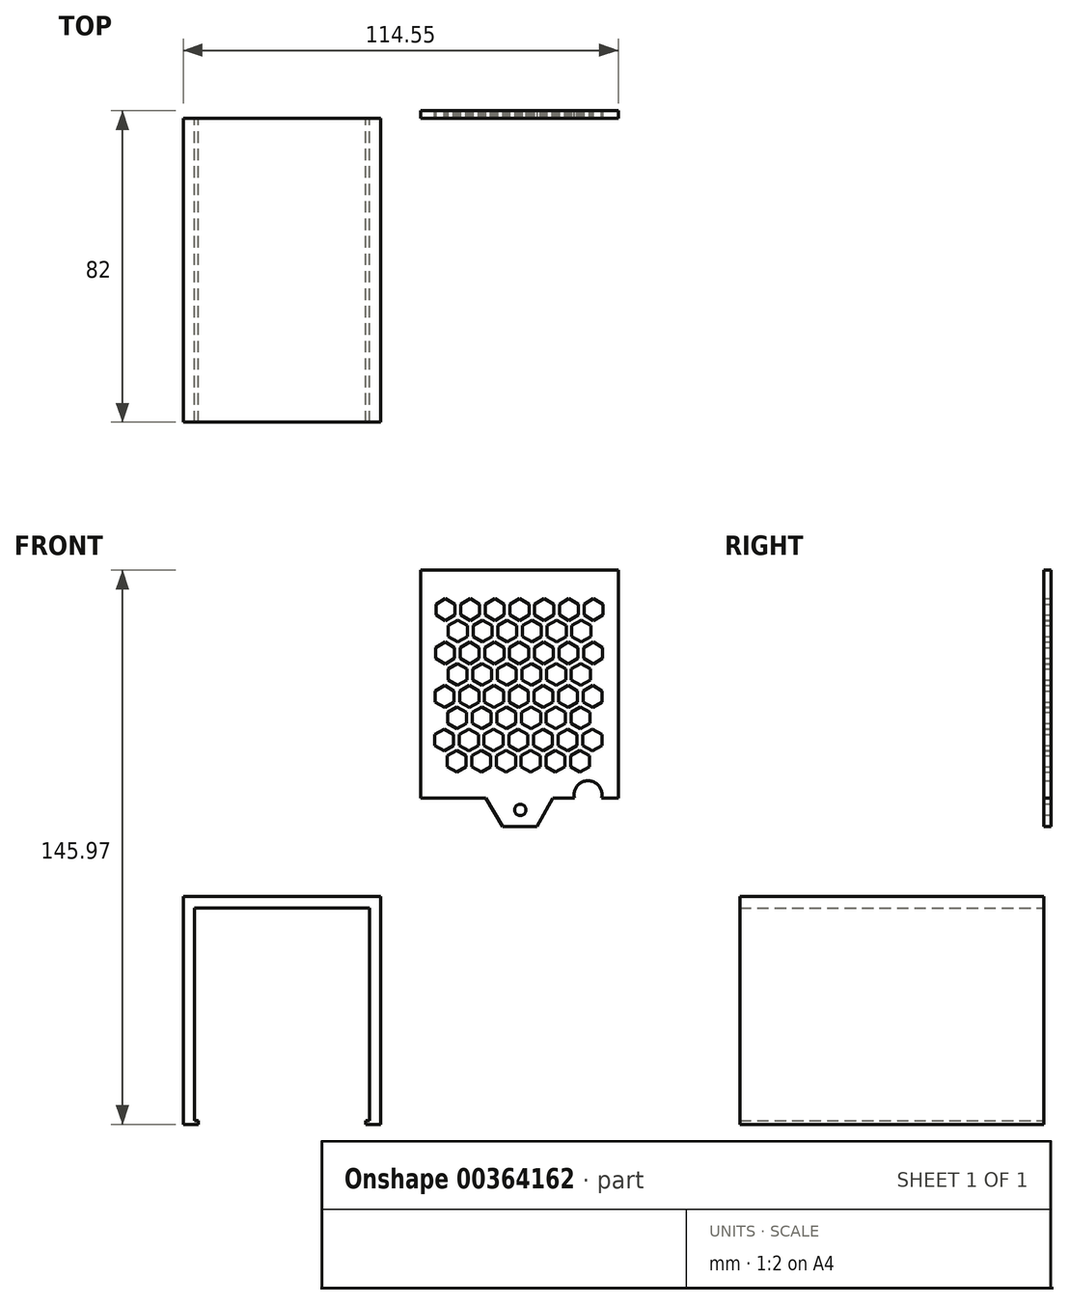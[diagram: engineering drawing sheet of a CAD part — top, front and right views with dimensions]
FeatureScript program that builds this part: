
annotation { "Feature Type Name" : "Feature", "Feature Type Description" : "" }
export const myFeature = defineFeature(function(context is Context, id is Id, definition is map)
    precondition{}
    {
        {
            var Q0;
            Q0=qCreatedBy(makeId("Front.planeOp"),FACE);
            var sketch = newSketch(context, id + "F0", { "sketchPlane" : qUnion([Q0])});
            skLineSegment(sketch, "E0", {"start": v(-25.2, -51.06) * mm, "end": v(-29.2, -51.06) * mm});
            skLineSegment(sketch, "E1", {"start": v(-29.2, -51.06) * mm, "end": v(-29.2, 8.94) * mm});
            skLineSegment(sketch, "E2", {"start": v(-29.2, 8.94) * mm, "end": v(22.8, 8.94) * mm});
            skLineSegment(sketch, "E3", {"start": v(22.8, 8.94) * mm, "end": v(22.8, -51.06) * mm});
            skLineSegment(sketch, "E4", {"start": v(22.8, -51.06) * mm, "end": v(18.8, -51.06) * mm});
            skLineSegment(sketch, "E5", {"start": v(18.8, -51.06) * mm, "end": v(18.8, -50.06) * mm});
            skLineSegment(sketch, "E6", {"start": v(18.8, -50.06) * mm, "end": v(19.8, -50.06) * mm});
            skLineSegment(sketch, "E7", {"start": v(19.8, -50.06) * mm, "end": v(19.8, 5.94) * mm});
            skLineSegment(sketch, "E8", {"start": v(19.8, 5.94) * mm, "end": v(-26.2, 5.94) * mm});
            skLineSegment(sketch, "E9", {"start": v(-26.2, 5.94) * mm, "end": v(-26.2, -50.06) * mm});
            skLineSegment(sketch, "E10", {"start": v(-26.2, -50.06) * mm, "end": v(-25.2, -50.06) * mm});
            skLineSegment(sketch, "E11", {"start": v(-25.2, -50.06) * mm, "end": v(-25.2, -51.06) * mm});
            skSolve(sketch);
        }
        {
            var Q0;
            Q0=makeQuery(id+"F0.imprint","IMPRINT",FACE,{"disambiguationData":[TD([[makeQuery(id+"F0.imprint","IMPRINT",EDGE,{"derivedFrom":sQuery(id+"F0.wireOp",EDGE,"E0")}),-1.0]])]});
            extrude(context, id + "F1", {"entities" : qUnion([Q0]), "depth" : 80 * mm});
        }
        {
            var Q0;
            Q0=qCreatedBy(makeId("Front.planeOp"),FACE);
            var sketch = newSketch(context, id + "F2", { "sketchPlane" : qUnion([Q0])});
            skLineSegment(sketch, "E12.bottom", {"start": v(85.34, 94.91) * mm, "end": v(33.34, 94.91) * mm});
            skLineSegment(sketch, "E12.top", {"start": v(85.34, 34.91) * mm, "end": v(33.34, 34.91) * mm});
            skLineSegment(sketch, "E12.left", {"start": v(85.34, 94.91) * mm, "end": v(85.34, 34.91) * mm});
            skLineSegment(sketch, "E12.right", {"start": v(33.34, 94.91) * mm, "end": v(33.34, 34.91) * mm});
            skSolve(sketch);
        }
        {
            var Q0;
            Q0=makeQuery(id+"F2.imprint","IMPRINT",FACE,{"disambiguationData":[TD([[makeQuery(id+"F2.imprint","IMPRINT",EDGE,{"derivedFrom":sQuery(id+"F2.wireOp",EDGE,"E12.bottom")}),1.0]])]});
            extrude(context, id + "F3", {"entities" : qUnion([Q0]), "oppositeDirection" : true, "depth" : 2 * mm});
        }
        {
            var Q0;
            Q0=makeQuery(id+"F3.opExtrude","CAP_FACE",FACE,{"disambiguationData":[OSD([sQuery(id+"F2.wireOp",EDGE,"E12.bottom"),sQuery(id+"F2.wireOp",EDGE,"E12.top"),sQuery(id+"F2.wireOp",EDGE,"E12.left"),sQuery(id+"F2.wireOp",EDGE,"E12.right")])],"isStart":false});
            var sketch = newSketch(context, id + "F4", { "sketchPlane" : qUnion([Q0])});
            skCircle(sketch, "E13.cCircle", {"center": v(-78.84, 84.53) * mm, "radius": 2.5 * mm, "construction": true});
            skLineSegment(sketch, "E13.0", {"start": v(-76.34, 83.08) * mm, "end": v(-78.84, 81.64) * mm});
            skLineSegment(sketch, "E13.1", {"start": v(-78.84, 81.64) * mm, "end": v(-81.34, 83.08) * mm});
            skLineSegment(sketch, "E13.2", {"start": v(-81.34, 83.08) * mm, "end": v(-81.34, 85.97) * mm});
            skLineSegment(sketch, "E13.3", {"start": v(-81.34, 85.97) * mm, "end": v(-78.84, 87.41) * mm});
            skLineSegment(sketch, "E13.4", {"start": v(-78.84, 87.41) * mm, "end": v(-76.34, 85.97) * mm});
            skLineSegment(sketch, "E13.5", {"start": v(-76.34, 85.97) * mm, "end": v(-76.34, 83.08) * mm});
            skPoint(sketch, "E13.0.midPoint", {"position": v(-77.6, 82.36) * mm});
            skLineSegment(sketch, "E14.1.0.0", {"start": v(-69.84, 85.97) * mm, "end": v(-69.84, 83.08) * mm});
            skLineSegment(sketch, "E14.1.0.1", {"start": v(-72.34, 87.41) * mm, "end": v(-69.84, 85.97) * mm});
            skLineSegment(sketch, "E14.1.0.2", {"start": v(-74.84, 85.97) * mm, "end": v(-72.34, 87.41) * mm});
            skLineSegment(sketch, "E14.1.0.3", {"start": v(-74.84, 83.08) * mm, "end": v(-74.84, 85.97) * mm});
            skLineSegment(sketch, "E14.1.0.4", {"start": v(-72.34, 81.64) * mm, "end": v(-74.84, 83.08) * mm});
            skLineSegment(sketch, "E14.1.0.5", {"start": v(-69.84, 83.08) * mm, "end": v(-72.34, 81.64) * mm});
            skCircle(sketch, "E14.1.0.6", {"center": v(-72.34, 84.53) * mm, "radius": 2.5 * mm, "construction": true});
            skPoint(sketch, "E14.1.0.7", {"position": v(-71.1, 82.36) * mm});
            skLineSegment(sketch, "E14.2.0.0", {"start": v(-63.34, 85.97) * mm, "end": v(-63.34, 83.08) * mm});
            skLineSegment(sketch, "E14.2.0.1", {"start": v(-65.84, 87.41) * mm, "end": v(-63.34, 85.97) * mm});
            skLineSegment(sketch, "E14.2.0.2", {"start": v(-68.34, 85.97) * mm, "end": v(-65.84, 87.41) * mm});
            skLineSegment(sketch, "E14.2.0.3", {"start": v(-68.34, 83.08) * mm, "end": v(-68.34, 85.97) * mm});
            skLineSegment(sketch, "E14.2.0.4", {"start": v(-65.84, 81.64) * mm, "end": v(-68.34, 83.08) * mm});
            skLineSegment(sketch, "E14.2.0.5", {"start": v(-63.34, 83.08) * mm, "end": v(-65.84, 81.64) * mm});
            skCircle(sketch, "E14.2.0.6", {"center": v(-65.84, 84.53) * mm, "radius": 2.5 * mm, "construction": true});
            skPoint(sketch, "E14.2.0.7", {"position": v(-64.6, 82.36) * mm});
            skLineSegment(sketch, "E14.3.0.0", {"start": v(-56.84, 85.97) * mm, "end": v(-56.84, 83.08) * mm});
            skLineSegment(sketch, "E14.3.0.1", {"start": v(-59.34, 87.41) * mm, "end": v(-56.84, 85.97) * mm});
            skLineSegment(sketch, "E14.3.0.2", {"start": v(-61.84, 85.97) * mm, "end": v(-59.34, 87.41) * mm});
            skLineSegment(sketch, "E14.3.0.3", {"start": v(-61.84, 83.08) * mm, "end": v(-61.84, 85.97) * mm});
            skLineSegment(sketch, "E14.3.0.4", {"start": v(-59.34, 81.64) * mm, "end": v(-61.84, 83.08) * mm});
            skLineSegment(sketch, "E14.3.0.5", {"start": v(-56.84, 83.08) * mm, "end": v(-59.34, 81.64) * mm});
            skCircle(sketch, "E14.3.0.6", {"center": v(-59.34, 84.53) * mm, "radius": 2.5 * mm, "construction": true});
            skPoint(sketch, "E14.3.0.7", {"position": v(-58.1, 82.36) * mm});
            skLineSegment(sketch, "E14.4.0.0", {"start": v(-50.34, 85.97) * mm, "end": v(-50.34, 83.08) * mm});
            skLineSegment(sketch, "E14.4.0.1", {"start": v(-52.84, 87.41) * mm, "end": v(-50.34, 85.97) * mm});
            skLineSegment(sketch, "E14.4.0.2", {"start": v(-55.34, 85.97) * mm, "end": v(-52.84, 87.41) * mm});
            skLineSegment(sketch, "E14.4.0.3", {"start": v(-55.34, 83.08) * mm, "end": v(-55.34, 85.97) * mm});
            skLineSegment(sketch, "E14.4.0.4", {"start": v(-52.84, 81.64) * mm, "end": v(-55.34, 83.08) * mm});
            skLineSegment(sketch, "E14.4.0.5", {"start": v(-50.34, 83.08) * mm, "end": v(-52.84, 81.64) * mm});
            skCircle(sketch, "E14.4.0.6", {"center": v(-52.84, 84.53) * mm, "radius": 2.5 * mm, "construction": true});
            skPoint(sketch, "E14.4.0.7", {"position": v(-51.6, 82.36) * mm});
            skLineSegment(sketch, "E14.5.0.0", {"start": v(-43.84, 85.97) * mm, "end": v(-43.84, 83.08) * mm});
            skLineSegment(sketch, "E14.5.0.1", {"start": v(-46.34, 87.41) * mm, "end": v(-43.84, 85.97) * mm});
            skLineSegment(sketch, "E14.5.0.2", {"start": v(-48.84, 85.97) * mm, "end": v(-46.34, 87.41) * mm});
            skLineSegment(sketch, "E14.5.0.3", {"start": v(-48.84, 83.08) * mm, "end": v(-48.84, 85.97) * mm});
            skLineSegment(sketch, "E14.5.0.4", {"start": v(-46.34, 81.64) * mm, "end": v(-48.84, 83.08) * mm});
            skLineSegment(sketch, "E14.5.0.5", {"start": v(-43.84, 83.08) * mm, "end": v(-46.34, 81.64) * mm});
            skCircle(sketch, "E14.5.0.6", {"center": v(-46.34, 84.53) * mm, "radius": 2.5 * mm, "construction": true});
            skPoint(sketch, "E14.5.0.7", {"position": v(-45.1, 82.36) * mm});
            skLineSegment(sketch, "E14.direction1", {"start": v(-81.34, 83.08) * mm, "end": v(-74.84, 83.08) * mm, "construction": true});
            skLineSegment(sketch, "E15.0.6.0", {"start": v(-37.34, 85.97) * mm, "end": v(-37.34, 83.08) * mm});
            skLineSegment(sketch, "E15.3.6.0", {"start": v(-39.84, 87.41) * mm, "end": v(-37.34, 85.97) * mm});
            skLineSegment(sketch, "E15.6.6.0", {"start": v(-42.34, 85.97) * mm, "end": v(-39.84, 87.41) * mm});
            skLineSegment(sketch, "E15.9.6.0", {"start": v(-42.34, 83.08) * mm, "end": v(-42.34, 85.97) * mm});
            skLineSegment(sketch, "E15.12.6.0", {"start": v(-39.84, 81.64) * mm, "end": v(-42.34, 83.08) * mm});
            skLineSegment(sketch, "E15.15.6.0", {"start": v(-37.34, 83.08) * mm, "end": v(-39.84, 81.64) * mm});
            skCircle(sketch, "E15.18.6.0", {"center": v(-39.84, 84.53) * mm, "radius": 2.5 * mm, "construction": true});
            skPoint(sketch, "E15.20.6.0", {"position": v(-38.6, 82.36) * mm});
            skLineSegment(sketch, "E16.1.0.0", {"start": v(-73.11, 80.33) * mm, "end": v(-73.11, 77.44) * mm});
            skPoint(sketch, "E16.1.0.1", {"position": v(-74.36, 76.72) * mm});
            skLineSegment(sketch, "E16.1.0.2", {"start": v(-75.61, 81.77) * mm, "end": v(-73.11, 80.33) * mm});
            skLineSegment(sketch, "E16.1.0.3", {"start": v(-78.11, 77.44) * mm, "end": v(-78.11, 80.33) * mm});
            skLineSegment(sketch, "E16.1.0.4", {"start": v(-75.61, 76) * mm, "end": v(-78.11, 77.44) * mm});
            skLineSegment(sketch, "E16.1.0.5", {"start": v(-78.11, 80.33) * mm, "end": v(-75.61, 81.77) * mm});
            skCircle(sketch, "E16.1.0.6", {"center": v(-75.61, 78.89) * mm, "radius": 2.5 * mm, "construction": true});
            skLineSegment(sketch, "E16.1.0.7", {"start": v(-73.11, 77.44) * mm, "end": v(-75.61, 76) * mm});
            skLineSegment(sketch, "E17.1.0.0", {"start": v(-66.61, 80.33) * mm, "end": v(-66.61, 77.44) * mm});
            skLineSegment(sketch, "E17.1.0.1", {"start": v(-69.11, 76) * mm, "end": v(-71.61, 77.44) * mm});
            skLineSegment(sketch, "E17.1.0.2", {"start": v(-71.61, 77.44) * mm, "end": v(-71.61, 80.33) * mm});
            skPoint(sketch, "E17.1.0.3", {"position": v(-67.86, 76.72) * mm});
            skLineSegment(sketch, "E17.1.0.4", {"start": v(-66.61, 77.44) * mm, "end": v(-69.11, 76) * mm});
            skLineSegment(sketch, "E17.1.0.5", {"start": v(-71.61, 80.33) * mm, "end": v(-69.11, 81.77) * mm});
            skLineSegment(sketch, "E17.1.0.6", {"start": v(-69.11, 81.77) * mm, "end": v(-66.61, 80.33) * mm});
            skLineSegment(sketch, "E17.2.0.0", {"start": v(-60.11, 80.33) * mm, "end": v(-60.11, 77.44) * mm});
            skLineSegment(sketch, "E17.2.0.1", {"start": v(-62.61, 76) * mm, "end": v(-65.11, 77.44) * mm});
            skLineSegment(sketch, "E17.2.0.2", {"start": v(-65.11, 77.44) * mm, "end": v(-65.11, 80.33) * mm});
            skPoint(sketch, "E17.2.0.3", {"position": v(-61.36, 76.72) * mm});
            skLineSegment(sketch, "E17.2.0.4", {"start": v(-60.11, 77.44) * mm, "end": v(-62.61, 76) * mm});
            skLineSegment(sketch, "E17.2.0.5", {"start": v(-65.11, 80.33) * mm, "end": v(-62.61, 81.77) * mm});
            skLineSegment(sketch, "E17.2.0.6", {"start": v(-62.61, 81.77) * mm, "end": v(-60.11, 80.33) * mm});
            skLineSegment(sketch, "E17.3.0.0", {"start": v(-53.61, 80.33) * mm, "end": v(-53.61, 77.44) * mm});
            skLineSegment(sketch, "E17.3.0.1", {"start": v(-56.11, 76) * mm, "end": v(-58.61, 77.44) * mm});
            skLineSegment(sketch, "E17.3.0.2", {"start": v(-58.61, 77.44) * mm, "end": v(-58.61, 80.33) * mm});
            skPoint(sketch, "E17.3.0.3", {"position": v(-54.86, 76.72) * mm});
            skLineSegment(sketch, "E17.3.0.4", {"start": v(-53.61, 77.44) * mm, "end": v(-56.11, 76) * mm});
            skLineSegment(sketch, "E17.3.0.5", {"start": v(-58.61, 80.33) * mm, "end": v(-56.11, 81.77) * mm});
            skLineSegment(sketch, "E17.3.0.6", {"start": v(-56.11, 81.77) * mm, "end": v(-53.61, 80.33) * mm});
            skLineSegment(sketch, "E17.4.0.0", {"start": v(-47.11, 80.33) * mm, "end": v(-47.11, 77.44) * mm});
            skLineSegment(sketch, "E17.4.0.1", {"start": v(-49.61, 76) * mm, "end": v(-52.11, 77.44) * mm});
            skLineSegment(sketch, "E17.4.0.2", {"start": v(-52.11, 77.44) * mm, "end": v(-52.11, 80.33) * mm});
            skPoint(sketch, "E17.4.0.3", {"position": v(-48.36, 76.72) * mm});
            skLineSegment(sketch, "E17.4.0.4", {"start": v(-47.11, 77.44) * mm, "end": v(-49.61, 76) * mm});
            skLineSegment(sketch, "E17.4.0.5", {"start": v(-52.11, 80.33) * mm, "end": v(-49.61, 81.77) * mm});
            skLineSegment(sketch, "E17.4.0.6", {"start": v(-49.61, 81.77) * mm, "end": v(-47.11, 80.33) * mm});
            skLineSegment(sketch, "E17.5.0.0", {"start": v(-40.61, 80.33) * mm, "end": v(-40.61, 77.44) * mm});
            skLineSegment(sketch, "E17.5.0.1", {"start": v(-43.11, 76) * mm, "end": v(-45.61, 77.44) * mm});
            skLineSegment(sketch, "E17.5.0.2", {"start": v(-45.61, 77.44) * mm, "end": v(-45.61, 80.33) * mm});
            skPoint(sketch, "E17.5.0.3", {"position": v(-41.86, 76.72) * mm});
            skLineSegment(sketch, "E17.5.0.4", {"start": v(-40.61, 77.44) * mm, "end": v(-43.11, 76) * mm});
            skLineSegment(sketch, "E17.5.0.5", {"start": v(-45.61, 80.33) * mm, "end": v(-43.11, 81.77) * mm});
            skLineSegment(sketch, "E17.5.0.6", {"start": v(-43.11, 81.77) * mm, "end": v(-40.61, 80.33) * mm});
            skLineSegment(sketch, "E17.direction1", {"start": v(-78.11, 77.44) * mm, "end": v(-71.61, 77.44) * mm, "construction": true});
            skLineSegment(sketch, "E18.1.0.0", {"start": v(-65.73, 70.2) * mm, "end": v(-68.23, 71.64) * mm});
            skLineSegment(sketch, "E18.1.0.1", {"start": v(-78.73, 70.2) * mm, "end": v(-81.23, 71.64) * mm});
            skCircle(sketch, "E18.1.0.2", {"center": v(-52.73, 73.08) * mm, "radius": 2.5 * mm, "construction": true});
            skLineSegment(sketch, "E18.1.0.3", {"start": v(-43, 64.56) * mm, "end": v(-45.5, 66) * mm});
            skLineSegment(sketch, "E18.1.0.4", {"start": v(-73, 68.89) * mm, "end": v(-73, 66) * mm});
            skPoint(sketch, "E18.1.0.5", {"position": v(-61.25, 65.28) * mm});
            skLineSegment(sketch, "E18.1.0.6", {"start": v(-65.73, 75.97) * mm, "end": v(-63.23, 74.53) * mm});
            skPoint(sketch, "E18.1.0.7", {"position": v(-54.75, 65.28) * mm});
            skCircle(sketch, "E18.1.0.8", {"center": v(-46.23, 73.08) * mm, "radius": 2.5 * mm, "construction": true});
            skLineSegment(sketch, "E18.1.0.9", {"start": v(-58.5, 68.89) * mm, "end": v(-56, 70.33) * mm});
            skLineSegment(sketch, "E18.1.0.10", {"start": v(-69, 64.56) * mm, "end": v(-71.5, 66) * mm});
            skLineSegment(sketch, "E18.1.0.11", {"start": v(-56, 70.33) * mm, "end": v(-53.5, 68.89) * mm});
            skPoint(sketch, "E18.1.0.12", {"position": v(-48.25, 65.28) * mm});
            skLineSegment(sketch, "E18.1.0.13", {"start": v(-81.23, 71.64) * mm, "end": v(-74.73, 71.64) * mm, "construction": true});
            skLineSegment(sketch, "E18.1.0.14", {"start": v(-75.5, 70.33) * mm, "end": v(-73, 68.89) * mm});
            skLineSegment(sketch, "E18.1.0.15", {"start": v(-39.73, 70.2) * mm, "end": v(-42.23, 71.64) * mm});
            skLineSegment(sketch, "E18.1.0.16", {"start": v(-55.23, 71.64) * mm, "end": v(-55.23, 74.53) * mm});
            skLineSegment(sketch, "E18.1.0.17", {"start": v(-78, 68.89) * mm, "end": v(-75.5, 70.33) * mm});
            skLineSegment(sketch, "E18.1.0.18", {"start": v(-43, 70.33) * mm, "end": v(-40.5, 68.89) * mm});
            skLineSegment(sketch, "E18.1.0.19", {"start": v(-59.23, 75.97) * mm, "end": v(-56.73, 74.53) * mm});
            skLineSegment(sketch, "E18.1.0.20", {"start": v(-56, 64.56) * mm, "end": v(-58.5, 66) * mm});
            skLineSegment(sketch, "E18.1.0.21", {"start": v(-60, 68.89) * mm, "end": v(-60, 66) * mm});
            skLineSegment(sketch, "E18.1.0.22", {"start": v(-52, 68.89) * mm, "end": v(-49.5, 70.33) * mm});
            skPoint(sketch, "E18.1.0.23", {"position": v(-41.75, 65.28) * mm});
            skLineSegment(sketch, "E18.1.0.24", {"start": v(-52.73, 70.2) * mm, "end": v(-55.23, 71.64) * mm});
            skLineSegment(sketch, "E18.1.0.25", {"start": v(-68.23, 74.53) * mm, "end": v(-65.73, 75.97) * mm});
            skLineSegment(sketch, "E18.1.0.26", {"start": v(-49.5, 70.33) * mm, "end": v(-47, 68.89) * mm});
            skCircle(sketch, "E18.1.0.27", {"center": v(-78.73, 73.08) * mm, "radius": 2.5 * mm, "construction": true});
            skPoint(sketch, "E18.1.0.28", {"position": v(-38.48, 70.92) * mm});
            skPoint(sketch, "E18.1.0.29", {"position": v(-57.98, 70.92) * mm});
            skLineSegment(sketch, "E18.1.0.30", {"start": v(-62.5, 64.56) * mm, "end": v(-65, 66) * mm});
            skLineSegment(sketch, "E18.1.0.31", {"start": v(-61.73, 74.53) * mm, "end": v(-59.23, 75.97) * mm});
            skLineSegment(sketch, "E18.1.0.32", {"start": v(-59.23, 70.2) * mm, "end": v(-61.73, 71.64) * mm});
            skLineSegment(sketch, "E18.1.0.33", {"start": v(-68.23, 71.64) * mm, "end": v(-68.23, 74.53) * mm});
            skLineSegment(sketch, "E18.1.0.34", {"start": v(-45.5, 66) * mm, "end": v(-45.5, 68.89) * mm});
            skLineSegment(sketch, "E18.1.0.35", {"start": v(-63.23, 74.53) * mm, "end": v(-63.23, 71.64) * mm});
            skLineSegment(sketch, "E18.1.0.36", {"start": v(-65, 68.89) * mm, "end": v(-62.5, 70.33) * mm});
            skLineSegment(sketch, "E18.1.0.37", {"start": v(-48.73, 74.53) * mm, "end": v(-46.23, 75.97) * mm});
            skPoint(sketch, "E18.1.0.38", {"position": v(-64.48, 70.92) * mm});
            skLineSegment(sketch, "E18.1.0.39", {"start": v(-78, 66) * mm, "end": v(-71.5, 66) * mm, "construction": true});
            skLineSegment(sketch, "E18.1.0.40", {"start": v(-72.23, 70.2) * mm, "end": v(-74.73, 71.64) * mm});
            skLineSegment(sketch, "E18.1.0.41", {"start": v(-78, 66) * mm, "end": v(-78, 68.89) * mm});
            skLineSegment(sketch, "E18.1.0.42", {"start": v(-62.5, 70.33) * mm, "end": v(-60, 68.89) * mm});
            skCircle(sketch, "E18.1.0.43", {"center": v(-65.73, 73.08) * mm, "radius": 2.5 * mm, "construction": true});
            skLineSegment(sketch, "E18.1.0.44", {"start": v(-46.23, 75.97) * mm, "end": v(-43.73, 74.53) * mm});
            skLineSegment(sketch, "E18.1.0.45", {"start": v(-42.23, 74.53) * mm, "end": v(-39.73, 75.97) * mm});
            skLineSegment(sketch, "E18.1.0.46", {"start": v(-45.5, 68.89) * mm, "end": v(-43, 70.33) * mm});
            skLineSegment(sketch, "E18.1.0.47", {"start": v(-69, 70.33) * mm, "end": v(-66.5, 68.89) * mm});
            skLineSegment(sketch, "E18.1.0.48", {"start": v(-37.23, 74.53) * mm, "end": v(-37.23, 71.64) * mm});
            skLineSegment(sketch, "E18.1.0.49", {"start": v(-55.23, 74.53) * mm, "end": v(-52.73, 75.97) * mm});
            skLineSegment(sketch, "E18.1.0.50", {"start": v(-75.5, 64.56) * mm, "end": v(-78, 66) * mm});
            skLineSegment(sketch, "E18.1.0.51", {"start": v(-58.5, 66) * mm, "end": v(-58.5, 68.89) * mm});
            skLineSegment(sketch, "E18.1.0.52", {"start": v(-42.23, 71.64) * mm, "end": v(-42.23, 74.53) * mm});
            skPoint(sketch, "E18.1.0.53", {"position": v(-74.25, 65.28) * mm});
            skLineSegment(sketch, "E18.1.0.54", {"start": v(-66.5, 68.89) * mm, "end": v(-66.5, 66) * mm});
            skPoint(sketch, "E18.1.0.55", {"position": v(-70.98, 70.92) * mm});
            skLineSegment(sketch, "E18.1.0.56", {"start": v(-71.5, 66) * mm, "end": v(-71.5, 68.89) * mm});
            skLineSegment(sketch, "E18.1.0.57", {"start": v(-52, 66) * mm, "end": v(-52, 68.89) * mm});
            skPoint(sketch, "E18.1.0.58", {"position": v(-44.98, 70.92) * mm});
            skLineSegment(sketch, "E18.1.0.59", {"start": v(-71.5, 68.89) * mm, "end": v(-69, 70.33) * mm});
            skLineSegment(sketch, "E18.1.0.60", {"start": v(-46.23, 70.2) * mm, "end": v(-48.73, 71.64) * mm});
            skLineSegment(sketch, "E18.1.0.61", {"start": v(-56.73, 74.53) * mm, "end": v(-56.73, 71.64) * mm});
            skPoint(sketch, "E18.1.0.62", {"position": v(-77.48, 70.92) * mm});
            skLineSegment(sketch, "E18.1.0.63", {"start": v(-74.73, 74.53) * mm, "end": v(-72.23, 75.97) * mm});
            skCircle(sketch, "E18.1.0.64", {"center": v(-39.73, 73.08) * mm, "radius": 2.5 * mm, "construction": true});
            skLineSegment(sketch, "E18.1.0.65", {"start": v(-61.73, 71.64) * mm, "end": v(-61.73, 74.53) * mm});
            skPoint(sketch, "E18.1.0.66", {"position": v(-67.75, 65.28) * mm});
            skLineSegment(sketch, "E18.1.0.67", {"start": v(-81.23, 71.64) * mm, "end": v(-81.23, 74.53) * mm});
            skPoint(sketch, "E18.1.0.68", {"position": v(-51.48, 70.92) * mm});
            skLineSegment(sketch, "E18.1.0.69", {"start": v(-72.23, 75.97) * mm, "end": v(-69.73, 74.53) * mm});
            skCircle(sketch, "E18.1.0.70", {"center": v(-59.23, 73.08) * mm, "radius": 2.5 * mm, "construction": true});
            skLineSegment(sketch, "E18.1.0.71", {"start": v(-53.5, 68.89) * mm, "end": v(-53.5, 66) * mm});
            skLineSegment(sketch, "E18.1.0.72", {"start": v(-65, 66) * mm, "end": v(-65, 68.89) * mm});
            skCircle(sketch, "E18.1.0.73", {"center": v(-75.5, 67.44) * mm, "radius": 2.5 * mm, "construction": true});
            skCircle(sketch, "E18.1.0.74", {"center": v(-72.23, 73.08) * mm, "radius": 2.5 * mm, "construction": true});
            skLineSegment(sketch, "E18.1.0.75", {"start": v(-47, 68.89) * mm, "end": v(-47, 66) * mm});
            skLineSegment(sketch, "E18.1.0.76", {"start": v(-39.73, 75.97) * mm, "end": v(-37.23, 74.53) * mm});
            skLineSegment(sketch, "E18.1.0.77", {"start": v(-81.23, 74.53) * mm, "end": v(-78.73, 75.97) * mm});
            skLineSegment(sketch, "E18.1.0.78", {"start": v(-40.5, 68.89) * mm, "end": v(-40.5, 66) * mm});
            skLineSegment(sketch, "E18.1.0.79", {"start": v(-49.5, 64.56) * mm, "end": v(-52, 66) * mm});
            skLineSegment(sketch, "E18.1.0.80", {"start": v(-73, 66) * mm, "end": v(-75.5, 64.56) * mm});
            skLineSegment(sketch, "E18.1.0.81", {"start": v(-53.5, 66) * mm, "end": v(-56, 64.56) * mm});
            skLineSegment(sketch, "E18.1.0.82", {"start": v(-43.73, 71.64) * mm, "end": v(-46.23, 70.2) * mm});
            skLineSegment(sketch, "E18.1.0.83", {"start": v(-76.23, 71.64) * mm, "end": v(-78.73, 70.2) * mm});
            skLineSegment(sketch, "E18.1.0.84", {"start": v(-43.73, 74.53) * mm, "end": v(-43.73, 71.64) * mm});
            skLineSegment(sketch, "E18.1.0.85", {"start": v(-50.23, 71.64) * mm, "end": v(-52.73, 70.2) * mm});
            skLineSegment(sketch, "E18.1.0.86", {"start": v(-56.73, 71.64) * mm, "end": v(-59.23, 70.2) * mm});
            skLineSegment(sketch, "E18.1.0.87", {"start": v(-63.23, 71.64) * mm, "end": v(-65.73, 70.2) * mm});
            skLineSegment(sketch, "E18.1.0.88", {"start": v(-48.73, 71.64) * mm, "end": v(-48.73, 74.53) * mm});
            skLineSegment(sketch, "E18.1.0.89", {"start": v(-37.23, 71.64) * mm, "end": v(-39.73, 70.2) * mm});
            skLineSegment(sketch, "E18.1.0.90", {"start": v(-76.23, 74.53) * mm, "end": v(-76.23, 71.64) * mm});
            skLineSegment(sketch, "E18.1.0.91", {"start": v(-52.73, 75.97) * mm, "end": v(-50.23, 74.53) * mm});
            skLineSegment(sketch, "E18.1.0.92", {"start": v(-69.73, 71.64) * mm, "end": v(-72.23, 70.2) * mm});
            skLineSegment(sketch, "E18.1.0.93", {"start": v(-69.73, 74.53) * mm, "end": v(-69.73, 71.64) * mm});
            skLineSegment(sketch, "E18.1.0.94", {"start": v(-66.5, 66) * mm, "end": v(-69, 64.56) * mm});
            skLineSegment(sketch, "E18.1.0.95", {"start": v(-40.5, 66) * mm, "end": v(-43, 64.56) * mm});
            skLineSegment(sketch, "E18.1.0.96", {"start": v(-47, 66) * mm, "end": v(-49.5, 64.56) * mm});
            skLineSegment(sketch, "E18.1.0.97", {"start": v(-74.73, 71.64) * mm, "end": v(-74.73, 74.53) * mm});
            skLineSegment(sketch, "E18.1.0.98", {"start": v(-50.23, 74.53) * mm, "end": v(-50.23, 71.64) * mm});
            skLineSegment(sketch, "E18.1.0.99", {"start": v(-60, 66) * mm, "end": v(-62.5, 64.56) * mm});
            skLineSegment(sketch, "E18.1.0.100", {"start": v(-78.73, 75.97) * mm, "end": v(-76.23, 74.53) * mm});
            skLineSegment(sketch, "E18.2.0.0", {"start": v(-65.62, 58.75) * mm, "end": v(-68.12, 60.2) * mm});
            skLineSegment(sketch, "E18.2.0.1", {"start": v(-78.62, 58.75) * mm, "end": v(-81.12, 60.2) * mm});
            skCircle(sketch, "E18.2.0.2", {"center": v(-52.62, 61.64) * mm, "radius": 2.5 * mm, "construction": true});
            skLineSegment(sketch, "E18.2.0.3", {"start": v(-42.89, 53.11) * mm, "end": v(-45.39, 54.56) * mm});
            skLineSegment(sketch, "E18.2.0.4", {"start": v(-72.89, 57.44) * mm, "end": v(-72.89, 54.56) * mm});
            skPoint(sketch, "E18.2.0.5", {"position": v(-61.14, 53.83) * mm});
            skLineSegment(sketch, "E18.2.0.6", {"start": v(-65.62, 64.53) * mm, "end": v(-63.12, 63.08) * mm});
            skPoint(sketch, "E18.2.0.7", {"position": v(-54.64, 53.83) * mm});
            skCircle(sketch, "E18.2.0.8", {"center": v(-46.12, 61.64) * mm, "radius": 2.5 * mm, "construction": true});
            skLineSegment(sketch, "E18.2.0.9", {"start": v(-58.39, 57.44) * mm, "end": v(-55.89, 58.89) * mm});
            skLineSegment(sketch, "E18.2.0.10", {"start": v(-68.89, 53.11) * mm, "end": v(-71.39, 54.56) * mm});
            skLineSegment(sketch, "E18.2.0.11", {"start": v(-55.89, 58.89) * mm, "end": v(-53.39, 57.44) * mm});
            skPoint(sketch, "E18.2.0.12", {"position": v(-48.14, 53.83) * mm});
            skLineSegment(sketch, "E18.2.0.13", {"start": v(-81.12, 60.2) * mm, "end": v(-74.62, 60.2) * mm, "construction": true});
            skLineSegment(sketch, "E18.2.0.14", {"start": v(-75.39, 58.89) * mm, "end": v(-72.89, 57.44) * mm});
            skLineSegment(sketch, "E18.2.0.15", {"start": v(-39.62, 58.75) * mm, "end": v(-42.12, 60.2) * mm});
            skLineSegment(sketch, "E18.2.0.16", {"start": v(-55.12, 60.2) * mm, "end": v(-55.12, 63.08) * mm});
            skLineSegment(sketch, "E18.2.0.17", {"start": v(-77.89, 57.44) * mm, "end": v(-75.39, 58.89) * mm});
            skLineSegment(sketch, "E18.2.0.18", {"start": v(-42.89, 58.89) * mm, "end": v(-40.39, 57.44) * mm});
            skLineSegment(sketch, "E18.2.0.19", {"start": v(-59.12, 64.53) * mm, "end": v(-56.62, 63.08) * mm});
            skLineSegment(sketch, "E18.2.0.20", {"start": v(-55.89, 53.11) * mm, "end": v(-58.39, 54.56) * mm});
            skLineSegment(sketch, "E18.2.0.21", {"start": v(-59.89, 57.44) * mm, "end": v(-59.89, 54.56) * mm});
            skLineSegment(sketch, "E18.2.0.22", {"start": v(-51.89, 57.44) * mm, "end": v(-49.39, 58.89) * mm});
            skPoint(sketch, "E18.2.0.23", {"position": v(-41.64, 53.83) * mm});
            skLineSegment(sketch, "E18.2.0.24", {"start": v(-52.62, 58.75) * mm, "end": v(-55.12, 60.2) * mm});
            skLineSegment(sketch, "E18.2.0.25", {"start": v(-68.12, 63.08) * mm, "end": v(-65.62, 64.53) * mm});
            skLineSegment(sketch, "E18.2.0.26", {"start": v(-49.39, 58.89) * mm, "end": v(-46.89, 57.44) * mm});
            skCircle(sketch, "E18.2.0.27", {"center": v(-78.62, 61.64) * mm, "radius": 2.5 * mm, "construction": true});
            skPoint(sketch, "E18.2.0.28", {"position": v(-38.37, 59.47) * mm});
            skPoint(sketch, "E18.2.0.29", {"position": v(-57.87, 59.47) * mm});
            skLineSegment(sketch, "E18.2.0.30", {"start": v(-62.39, 53.11) * mm, "end": v(-64.89, 54.56) * mm});
            skLineSegment(sketch, "E18.2.0.31", {"start": v(-61.62, 63.08) * mm, "end": v(-59.12, 64.53) * mm});
            skLineSegment(sketch, "E18.2.0.32", {"start": v(-59.12, 58.75) * mm, "end": v(-61.62, 60.2) * mm});
            skLineSegment(sketch, "E18.2.0.33", {"start": v(-68.12, 60.2) * mm, "end": v(-68.12, 63.08) * mm});
            skLineSegment(sketch, "E18.2.0.34", {"start": v(-45.39, 54.56) * mm, "end": v(-45.39, 57.44) * mm});
            skLineSegment(sketch, "E18.2.0.35", {"start": v(-63.12, 63.08) * mm, "end": v(-63.12, 60.2) * mm});
            skLineSegment(sketch, "E18.2.0.36", {"start": v(-64.89, 57.44) * mm, "end": v(-62.39, 58.89) * mm});
            skLineSegment(sketch, "E18.2.0.37", {"start": v(-48.62, 63.08) * mm, "end": v(-46.12, 64.53) * mm});
            skPoint(sketch, "E18.2.0.38", {"position": v(-64.37, 59.47) * mm});
            skLineSegment(sketch, "E18.2.0.39", {"start": v(-77.89, 54.56) * mm, "end": v(-71.39, 54.56) * mm, "construction": true});
            skLineSegment(sketch, "E18.2.0.40", {"start": v(-72.12, 58.75) * mm, "end": v(-74.62, 60.2) * mm});
            skLineSegment(sketch, "E18.2.0.41", {"start": v(-77.89, 54.56) * mm, "end": v(-77.89, 57.44) * mm});
            skLineSegment(sketch, "E18.2.0.42", {"start": v(-62.39, 58.89) * mm, "end": v(-59.89, 57.44) * mm});
            skCircle(sketch, "E18.2.0.43", {"center": v(-65.62, 61.64) * mm, "radius": 2.5 * mm, "construction": true});
            skLineSegment(sketch, "E18.2.0.44", {"start": v(-46.12, 64.53) * mm, "end": v(-43.62, 63.08) * mm});
            skLineSegment(sketch, "E18.2.0.45", {"start": v(-42.12, 63.08) * mm, "end": v(-39.62, 64.53) * mm});
            skLineSegment(sketch, "E18.2.0.46", {"start": v(-45.39, 57.44) * mm, "end": v(-42.89, 58.89) * mm});
            skLineSegment(sketch, "E18.2.0.47", {"start": v(-68.89, 58.89) * mm, "end": v(-66.39, 57.44) * mm});
            skLineSegment(sketch, "E18.2.0.48", {"start": v(-37.12, 63.08) * mm, "end": v(-37.12, 60.2) * mm});
            skLineSegment(sketch, "E18.2.0.49", {"start": v(-55.12, 63.08) * mm, "end": v(-52.62, 64.53) * mm});
            skLineSegment(sketch, "E18.2.0.50", {"start": v(-75.39, 53.11) * mm, "end": v(-77.89, 54.56) * mm});
            skLineSegment(sketch, "E18.2.0.51", {"start": v(-58.39, 54.56) * mm, "end": v(-58.39, 57.44) * mm});
            skLineSegment(sketch, "E18.2.0.52", {"start": v(-42.12, 60.2) * mm, "end": v(-42.12, 63.08) * mm});
            skPoint(sketch, "E18.2.0.53", {"position": v(-74.14, 53.83) * mm});
            skLineSegment(sketch, "E18.2.0.54", {"start": v(-66.39, 57.44) * mm, "end": v(-66.39, 54.56) * mm});
            skPoint(sketch, "E18.2.0.55", {"position": v(-70.87, 59.47) * mm});
            skLineSegment(sketch, "E18.2.0.56", {"start": v(-71.39, 54.56) * mm, "end": v(-71.39, 57.44) * mm});
            skLineSegment(sketch, "E18.2.0.57", {"start": v(-51.89, 54.56) * mm, "end": v(-51.89, 57.44) * mm});
            skPoint(sketch, "E18.2.0.58", {"position": v(-44.87, 59.47) * mm});
            skLineSegment(sketch, "E18.2.0.59", {"start": v(-71.39, 57.44) * mm, "end": v(-68.89, 58.89) * mm});
            skLineSegment(sketch, "E18.2.0.60", {"start": v(-46.12, 58.75) * mm, "end": v(-48.62, 60.2) * mm});
            skLineSegment(sketch, "E18.2.0.61", {"start": v(-56.62, 63.08) * mm, "end": v(-56.62, 60.2) * mm});
            skPoint(sketch, "E18.2.0.62", {"position": v(-77.37, 59.47) * mm});
            skLineSegment(sketch, "E18.2.0.63", {"start": v(-74.62, 63.08) * mm, "end": v(-72.12, 64.53) * mm});
            skCircle(sketch, "E18.2.0.64", {"center": v(-39.62, 61.64) * mm, "radius": 2.5 * mm, "construction": true});
            skLineSegment(sketch, "E18.2.0.65", {"start": v(-61.62, 60.2) * mm, "end": v(-61.62, 63.08) * mm});
            skPoint(sketch, "E18.2.0.66", {"position": v(-67.64, 53.83) * mm});
            skLineSegment(sketch, "E18.2.0.67", {"start": v(-81.12, 60.2) * mm, "end": v(-81.12, 63.08) * mm});
            skPoint(sketch, "E18.2.0.68", {"position": v(-51.37, 59.47) * mm});
            skLineSegment(sketch, "E18.2.0.69", {"start": v(-72.12, 64.53) * mm, "end": v(-69.62, 63.08) * mm});
            skCircle(sketch, "E18.2.0.70", {"center": v(-59.12, 61.64) * mm, "radius": 2.5 * mm, "construction": true});
            skLineSegment(sketch, "E18.2.0.71", {"start": v(-53.39, 57.44) * mm, "end": v(-53.39, 54.56) * mm});
            skLineSegment(sketch, "E18.2.0.72", {"start": v(-64.89, 54.56) * mm, "end": v(-64.89, 57.44) * mm});
            skCircle(sketch, "E18.2.0.73", {"center": v(-75.39, 56) * mm, "radius": 2.5 * mm, "construction": true});
            skCircle(sketch, "E18.2.0.74", {"center": v(-72.12, 61.64) * mm, "radius": 2.5 * mm, "construction": true});
            skLineSegment(sketch, "E18.2.0.75", {"start": v(-46.89, 57.44) * mm, "end": v(-46.89, 54.56) * mm});
            skLineSegment(sketch, "E18.2.0.76", {"start": v(-39.62, 64.53) * mm, "end": v(-37.12, 63.08) * mm});
            skLineSegment(sketch, "E18.2.0.77", {"start": v(-81.12, 63.08) * mm, "end": v(-78.62, 64.53) * mm});
            skLineSegment(sketch, "E18.2.0.78", {"start": v(-40.39, 57.44) * mm, "end": v(-40.39, 54.56) * mm});
            skLineSegment(sketch, "E18.2.0.79", {"start": v(-49.39, 53.11) * mm, "end": v(-51.89, 54.56) * mm});
            skLineSegment(sketch, "E18.2.0.80", {"start": v(-72.89, 54.56) * mm, "end": v(-75.39, 53.11) * mm});
            skLineSegment(sketch, "E18.2.0.81", {"start": v(-53.39, 54.56) * mm, "end": v(-55.89, 53.11) * mm});
            skLineSegment(sketch, "E18.2.0.82", {"start": v(-43.62, 60.2) * mm, "end": v(-46.12, 58.75) * mm});
            skLineSegment(sketch, "E18.2.0.83", {"start": v(-76.12, 60.2) * mm, "end": v(-78.62, 58.75) * mm});
            skLineSegment(sketch, "E18.2.0.84", {"start": v(-43.62, 63.08) * mm, "end": v(-43.62, 60.2) * mm});
            skLineSegment(sketch, "E18.2.0.85", {"start": v(-50.12, 60.2) * mm, "end": v(-52.62, 58.75) * mm});
            skLineSegment(sketch, "E18.2.0.86", {"start": v(-56.62, 60.2) * mm, "end": v(-59.12, 58.75) * mm});
            skLineSegment(sketch, "E18.2.0.87", {"start": v(-63.12, 60.2) * mm, "end": v(-65.62, 58.75) * mm});
            skLineSegment(sketch, "E18.2.0.88", {"start": v(-48.62, 60.2) * mm, "end": v(-48.62, 63.08) * mm});
            skLineSegment(sketch, "E18.2.0.89", {"start": v(-37.12, 60.2) * mm, "end": v(-39.62, 58.75) * mm});
            skLineSegment(sketch, "E18.2.0.90", {"start": v(-76.12, 63.08) * mm, "end": v(-76.12, 60.2) * mm});
            skLineSegment(sketch, "E18.2.0.91", {"start": v(-52.62, 64.53) * mm, "end": v(-50.12, 63.08) * mm});
            skLineSegment(sketch, "E18.2.0.92", {"start": v(-69.62, 60.2) * mm, "end": v(-72.12, 58.75) * mm});
            skLineSegment(sketch, "E18.2.0.93", {"start": v(-69.62, 63.08) * mm, "end": v(-69.62, 60.2) * mm});
            skLineSegment(sketch, "E18.2.0.94", {"start": v(-66.39, 54.56) * mm, "end": v(-68.89, 53.11) * mm});
            skLineSegment(sketch, "E18.2.0.95", {"start": v(-40.39, 54.56) * mm, "end": v(-42.89, 53.11) * mm});
            skLineSegment(sketch, "E18.2.0.96", {"start": v(-46.89, 54.56) * mm, "end": v(-49.39, 53.11) * mm});
            skLineSegment(sketch, "E18.2.0.97", {"start": v(-74.62, 60.2) * mm, "end": v(-74.62, 63.08) * mm});
            skLineSegment(sketch, "E18.2.0.98", {"start": v(-50.12, 63.08) * mm, "end": v(-50.12, 60.2) * mm});
            skLineSegment(sketch, "E18.2.0.99", {"start": v(-59.89, 54.56) * mm, "end": v(-62.39, 53.11) * mm});
            skLineSegment(sketch, "E18.2.0.100", {"start": v(-78.62, 64.53) * mm, "end": v(-76.12, 63.08) * mm});
            skLineSegment(sketch, "E18.3.0.0", {"start": v(-65.51, 47.3) * mm, "end": v(-68.01, 48.75) * mm});
            skLineSegment(sketch, "E18.3.0.1", {"start": v(-78.51, 47.3) * mm, "end": v(-81.01, 48.75) * mm});
            skCircle(sketch, "E18.3.0.2", {"center": v(-52.51, 50.2) * mm, "radius": 2.5 * mm, "construction": true});
            skLineSegment(sketch, "E18.3.0.3", {"start": v(-42.78, 41.67) * mm, "end": v(-45.28, 43.11) * mm});
            skLineSegment(sketch, "E18.3.0.4", {"start": v(-72.78, 46) * mm, "end": v(-72.78, 43.11) * mm});
            skPoint(sketch, "E18.3.0.5", {"position": v(-61.03, 42.4) * mm});
            skLineSegment(sketch, "E18.3.0.6", {"start": v(-65.51, 53.08) * mm, "end": v(-63.01, 51.64) * mm});
            skPoint(sketch, "E18.3.0.7", {"position": v(-54.53, 42.4) * mm});
            skCircle(sketch, "E18.3.0.8", {"center": v(-46.01, 50.2) * mm, "radius": 2.5 * mm, "construction": true});
            skLineSegment(sketch, "E18.3.0.9", {"start": v(-58.28, 46) * mm, "end": v(-55.78, 47.44) * mm});
            skLineSegment(sketch, "E18.3.0.10", {"start": v(-68.78, 41.67) * mm, "end": v(-71.28, 43.11) * mm});
            skLineSegment(sketch, "E18.3.0.11", {"start": v(-55.78, 47.44) * mm, "end": v(-53.28, 46) * mm});
            skPoint(sketch, "E18.3.0.12", {"position": v(-48.03, 42.4) * mm});
            skLineSegment(sketch, "E18.3.0.13", {"start": v(-81.01, 48.75) * mm, "end": v(-74.51, 48.75) * mm, "construction": true});
            skLineSegment(sketch, "E18.3.0.14", {"start": v(-75.28, 47.44) * mm, "end": v(-72.78, 46) * mm});
            skLineSegment(sketch, "E18.3.0.15", {"start": v(-39.51, 47.3) * mm, "end": v(-42.01, 48.75) * mm});
            skLineSegment(sketch, "E18.3.0.16", {"start": v(-55.01, 48.75) * mm, "end": v(-55.01, 51.64) * mm});
            skLineSegment(sketch, "E18.3.0.17", {"start": v(-77.78, 46) * mm, "end": v(-75.28, 47.44) * mm});
            skLineSegment(sketch, "E18.3.0.18", {"start": v(-42.78, 47.44) * mm, "end": v(-40.28, 46) * mm});
            skLineSegment(sketch, "E18.3.0.19", {"start": v(-59.01, 53.08) * mm, "end": v(-56.51, 51.64) * mm});
            skLineSegment(sketch, "E18.3.0.20", {"start": v(-55.78, 41.67) * mm, "end": v(-58.28, 43.11) * mm});
            skLineSegment(sketch, "E18.3.0.21", {"start": v(-59.78, 46) * mm, "end": v(-59.78, 43.11) * mm});
            skLineSegment(sketch, "E18.3.0.22", {"start": v(-51.78, 46) * mm, "end": v(-49.28, 47.44) * mm});
            skPoint(sketch, "E18.3.0.23", {"position": v(-41.53, 42.4) * mm});
            skLineSegment(sketch, "E18.3.0.24", {"start": v(-52.51, 47.3) * mm, "end": v(-55.01, 48.75) * mm});
            skLineSegment(sketch, "E18.3.0.25", {"start": v(-68.01, 51.64) * mm, "end": v(-65.51, 53.08) * mm});
            skLineSegment(sketch, "E18.3.0.26", {"start": v(-49.28, 47.44) * mm, "end": v(-46.78, 46) * mm});
            skCircle(sketch, "E18.3.0.27", {"center": v(-78.51, 50.2) * mm, "radius": 2.5 * mm, "construction": true});
            skPoint(sketch, "E18.3.0.28", {"position": v(-38.26, 48.03) * mm});
            skPoint(sketch, "E18.3.0.29", {"position": v(-57.76, 48.03) * mm});
            skLineSegment(sketch, "E18.3.0.30", {"start": v(-62.28, 41.67) * mm, "end": v(-64.78, 43.11) * mm});
            skLineSegment(sketch, "E18.3.0.31", {"start": v(-61.51, 51.64) * mm, "end": v(-59.01, 53.08) * mm});
            skLineSegment(sketch, "E18.3.0.32", {"start": v(-59.01, 47.3) * mm, "end": v(-61.51, 48.75) * mm});
            skLineSegment(sketch, "E18.3.0.33", {"start": v(-68.01, 48.75) * mm, "end": v(-68.01, 51.64) * mm});
            skLineSegment(sketch, "E18.3.0.34", {"start": v(-45.28, 43.11) * mm, "end": v(-45.28, 46) * mm});
            skLineSegment(sketch, "E18.3.0.35", {"start": v(-63.01, 51.64) * mm, "end": v(-63.01, 48.75) * mm});
            skLineSegment(sketch, "E18.3.0.36", {"start": v(-64.78, 46) * mm, "end": v(-62.28, 47.44) * mm});
            skLineSegment(sketch, "E18.3.0.37", {"start": v(-48.51, 51.64) * mm, "end": v(-46.01, 53.08) * mm});
            skPoint(sketch, "E18.3.0.38", {"position": v(-64.26, 48.03) * mm});
            skLineSegment(sketch, "E18.3.0.39", {"start": v(-77.78, 43.11) * mm, "end": v(-71.28, 43.11) * mm, "construction": true});
            skLineSegment(sketch, "E18.3.0.40", {"start": v(-72.01, 47.3) * mm, "end": v(-74.51, 48.75) * mm});
            skLineSegment(sketch, "E18.3.0.41", {"start": v(-77.78, 43.11) * mm, "end": v(-77.78, 46) * mm});
            skLineSegment(sketch, "E18.3.0.42", {"start": v(-62.28, 47.44) * mm, "end": v(-59.78, 46) * mm});
            skCircle(sketch, "E18.3.0.43", {"center": v(-65.51, 50.2) * mm, "radius": 2.5 * mm, "construction": true});
            skLineSegment(sketch, "E18.3.0.44", {"start": v(-46.01, 53.08) * mm, "end": v(-43.51, 51.64) * mm});
            skLineSegment(sketch, "E18.3.0.45", {"start": v(-42.01, 51.64) * mm, "end": v(-39.51, 53.08) * mm});
            skLineSegment(sketch, "E18.3.0.46", {"start": v(-45.28, 46) * mm, "end": v(-42.78, 47.44) * mm});
            skLineSegment(sketch, "E18.3.0.47", {"start": v(-68.78, 47.44) * mm, "end": v(-66.28, 46) * mm});
            skLineSegment(sketch, "E18.3.0.48", {"start": v(-37.01, 51.64) * mm, "end": v(-37.01, 48.75) * mm});
            skLineSegment(sketch, "E18.3.0.49", {"start": v(-55.01, 51.64) * mm, "end": v(-52.51, 53.08) * mm});
            skLineSegment(sketch, "E18.3.0.50", {"start": v(-75.28, 41.67) * mm, "end": v(-77.78, 43.11) * mm});
            skLineSegment(sketch, "E18.3.0.51", {"start": v(-58.28, 43.11) * mm, "end": v(-58.28, 46) * mm});
            skLineSegment(sketch, "E18.3.0.52", {"start": v(-42.01, 48.75) * mm, "end": v(-42.01, 51.64) * mm});
            skPoint(sketch, "E18.3.0.53", {"position": v(-74.03, 42.4) * mm});
            skLineSegment(sketch, "E18.3.0.54", {"start": v(-66.28, 46) * mm, "end": v(-66.28, 43.11) * mm});
            skPoint(sketch, "E18.3.0.55", {"position": v(-70.76, 48.03) * mm});
            skLineSegment(sketch, "E18.3.0.56", {"start": v(-71.28, 43.11) * mm, "end": v(-71.28, 46) * mm});
            skLineSegment(sketch, "E18.3.0.57", {"start": v(-51.78, 43.11) * mm, "end": v(-51.78, 46) * mm});
            skPoint(sketch, "E18.3.0.58", {"position": v(-44.76, 48.03) * mm});
            skLineSegment(sketch, "E18.3.0.59", {"start": v(-71.28, 46) * mm, "end": v(-68.78, 47.44) * mm});
            skLineSegment(sketch, "E18.3.0.60", {"start": v(-46.01, 47.3) * mm, "end": v(-48.51, 48.75) * mm});
            skLineSegment(sketch, "E18.3.0.61", {"start": v(-56.51, 51.64) * mm, "end": v(-56.51, 48.75) * mm});
            skPoint(sketch, "E18.3.0.62", {"position": v(-77.26, 48.03) * mm});
            skLineSegment(sketch, "E18.3.0.63", {"start": v(-74.51, 51.64) * mm, "end": v(-72.01, 53.08) * mm});
            skCircle(sketch, "E18.3.0.64", {"center": v(-39.51, 50.2) * mm, "radius": 2.5 * mm, "construction": true});
            skLineSegment(sketch, "E18.3.0.65", {"start": v(-61.51, 48.75) * mm, "end": v(-61.51, 51.64) * mm});
            skPoint(sketch, "E18.3.0.66", {"position": v(-67.53, 42.4) * mm});
            skLineSegment(sketch, "E18.3.0.67", {"start": v(-81.01, 48.75) * mm, "end": v(-81.01, 51.64) * mm});
            skPoint(sketch, "E18.3.0.68", {"position": v(-51.26, 48.03) * mm});
            skLineSegment(sketch, "E18.3.0.69", {"start": v(-72.01, 53.08) * mm, "end": v(-69.51, 51.64) * mm});
            skCircle(sketch, "E18.3.0.70", {"center": v(-59.01, 50.2) * mm, "radius": 2.5 * mm, "construction": true});
            skLineSegment(sketch, "E18.3.0.71", {"start": v(-53.28, 46) * mm, "end": v(-53.28, 43.11) * mm});
            skLineSegment(sketch, "E18.3.0.72", {"start": v(-64.78, 43.11) * mm, "end": v(-64.78, 46) * mm});
            skCircle(sketch, "E18.3.0.73", {"center": v(-75.28, 44.56) * mm, "radius": 2.5 * mm, "construction": true});
            skCircle(sketch, "E18.3.0.74", {"center": v(-72.01, 50.2) * mm, "radius": 2.5 * mm, "construction": true});
            skLineSegment(sketch, "E18.3.0.75", {"start": v(-46.78, 46) * mm, "end": v(-46.78, 43.11) * mm});
            skLineSegment(sketch, "E18.3.0.76", {"start": v(-39.51, 53.08) * mm, "end": v(-37.01, 51.64) * mm});
            skLineSegment(sketch, "E18.3.0.77", {"start": v(-81.01, 51.64) * mm, "end": v(-78.51, 53.08) * mm});
            skLineSegment(sketch, "E18.3.0.78", {"start": v(-40.28, 46) * mm, "end": v(-40.28, 43.11) * mm});
            skLineSegment(sketch, "E18.3.0.79", {"start": v(-49.28, 41.67) * mm, "end": v(-51.78, 43.11) * mm});
            skLineSegment(sketch, "E18.3.0.80", {"start": v(-72.78, 43.11) * mm, "end": v(-75.28, 41.67) * mm});
            skLineSegment(sketch, "E18.3.0.81", {"start": v(-53.28, 43.11) * mm, "end": v(-55.78, 41.67) * mm});
            skLineSegment(sketch, "E18.3.0.82", {"start": v(-43.51, 48.75) * mm, "end": v(-46.01, 47.3) * mm});
            skLineSegment(sketch, "E18.3.0.83", {"start": v(-76.01, 48.75) * mm, "end": v(-78.51, 47.3) * mm});
            skLineSegment(sketch, "E18.3.0.84", {"start": v(-43.51, 51.64) * mm, "end": v(-43.51, 48.75) * mm});
            skLineSegment(sketch, "E18.3.0.85", {"start": v(-50.01, 48.75) * mm, "end": v(-52.51, 47.3) * mm});
            skLineSegment(sketch, "E18.3.0.86", {"start": v(-56.51, 48.75) * mm, "end": v(-59.01, 47.3) * mm});
            skLineSegment(sketch, "E18.3.0.87", {"start": v(-63.01, 48.75) * mm, "end": v(-65.51, 47.3) * mm});
            skLineSegment(sketch, "E18.3.0.88", {"start": v(-48.51, 48.75) * mm, "end": v(-48.51, 51.64) * mm});
            skLineSegment(sketch, "E18.3.0.89", {"start": v(-37.01, 48.75) * mm, "end": v(-39.51, 47.3) * mm});
            skLineSegment(sketch, "E18.3.0.90", {"start": v(-76.01, 51.64) * mm, "end": v(-76.01, 48.75) * mm});
            skLineSegment(sketch, "E18.3.0.91", {"start": v(-52.51, 53.08) * mm, "end": v(-50.01, 51.64) * mm});
            skLineSegment(sketch, "E18.3.0.92", {"start": v(-69.51, 48.75) * mm, "end": v(-72.01, 47.3) * mm});
            skLineSegment(sketch, "E18.3.0.93", {"start": v(-69.51, 51.64) * mm, "end": v(-69.51, 48.75) * mm});
            skLineSegment(sketch, "E18.3.0.94", {"start": v(-66.28, 43.11) * mm, "end": v(-68.78, 41.67) * mm});
            skLineSegment(sketch, "E18.3.0.95", {"start": v(-40.28, 43.11) * mm, "end": v(-42.78, 41.67) * mm});
            skLineSegment(sketch, "E18.3.0.96", {"start": v(-46.78, 43.11) * mm, "end": v(-49.28, 41.67) * mm});
            skLineSegment(sketch, "E18.3.0.97", {"start": v(-74.51, 48.75) * mm, "end": v(-74.51, 51.64) * mm});
            skLineSegment(sketch, "E18.3.0.98", {"start": v(-50.01, 51.64) * mm, "end": v(-50.01, 48.75) * mm});
            skLineSegment(sketch, "E18.3.0.99", {"start": v(-59.78, 43.11) * mm, "end": v(-62.28, 41.67) * mm});
            skLineSegment(sketch, "E18.3.0.100", {"start": v(-78.51, 53.08) * mm, "end": v(-76.01, 51.64) * mm});
            skLineSegment(sketch, "E18.direction1", {"start": v(-78.11, 77.44) * mm, "end": v(-78, 66) * mm, "construction": true});
            skSolve(sketch);
        }
        {
            var Q0;
            Q0=qSketchRegion(id+"F4",true);
            extrude(context, id + "F5", {"entities" : qUnion([Q0]), "operationType" : NewBodyOperationType.REMOVE, "oppositeDirection" : true, "depth" : 2 * mm});
        }
        {
            var Q0;
            Q0=qCreatedBy(makeId("Front.planeOp"),FACE);
            var sketch = newSketch(context, id + "F6", { "sketchPlane" : qUnion([Q0])});
            skLineSegment(sketch, "E19.0", {"start": v(63.93, 27.37) * mm, "end": v(54.87, 27.37) * mm});
            skLineSegment(sketch, "E19.1", {"start": v(54.87, 27.37) * mm, "end": v(50.35, 35.21) * mm});
            skLineSegment(sketch, "E19.5", {"start": v(68.35, 35.21) * mm, "end": v(63.93, 27.37) * mm});
            skLineSegment(sketch, "E20", {"start": v(68.35, 35.21) * mm, "end": v(50.35, 35.21) * mm});
            skCircle(sketch, "E21", {"center": v(59.54, 31.74) * mm, "radius": 1.5 * mm});
            skSolve(sketch);
        }
        {
            var Q0;
            Q0=makeQuery(id+"F6.imprint","IMPRINT",FACE,{"disambiguationData":[TD([[makeQuery(id+"F6.imprint","IMPRINT",EDGE,{"derivedFrom":sQuery(id+"F6.wireOp",EDGE,"E19.0")}),-1.0]])]});
            extrude(context, id + "F7", {"entities" : qUnion([Q0]), "operationType" : NewBodyOperationType.ADD, "oppositeDirection" : true, "depth" : 2 * mm});
        }
        {
            var Q0;
            Q0=makeQuery(id+"F7.boolean.opBoolean","MERGE",FACE,{"derivedFrom":[makeQuery(id+"F3.opExtrude","CAP_FACE",FACE,{"disambiguationData":[OSD([sQuery(id+"F2.wireOp",EDGE,"E12.bottom"),sQuery(id+"F2.wireOp",EDGE,"E12.top"),sQuery(id+"F2.wireOp",EDGE,"E12.left"),sQuery(id+"F2.wireOp",EDGE,"E12.right")])],"isStart":false}),makeQuery(id+"F7.opExtrude","CAP_FACE",FACE,{"disambiguationData":[OSD([sQuery(id+"F6.wireOp",EDGE,"E19.0"),sQuery(id+"F6.wireOp",EDGE,"E19.1"),sQuery(id+"F6.wireOp",EDGE,"E19.5"),sQuery(id+"F6.wireOp",EDGE,"E20"),sQuery(id+"F6.wireOp",EDGE,"E21")])],"isStart":false})]});
            var sketch = newSketch(context, id + "F8", { "sketchPlane" : qUnion([Q0])});
            skArc(sketch, "E22", {"start": v(-73.77, 34.91) * mm, "mid": v(-77.38, 39.43) * mm, "end": v(-81, 34.91) * mm});
            skSolve(sketch);
        }
        {
            var Q0;
            {var subQ0=sQuery(id+"F8.wireOp",EDGE,"E22");Q0=makeQuery(id+"F8.imprint","IMPRINT",FACE,{"disambiguationData":[TD([[makeQuery(id+"F8.imprint","IMPRINT",EDGE,{"derivedFrom":subQ0}),1.0]])]});}
            var Q1;
            Q1=sQuery(id+"F8.wireOp",EDGE,"E22");
            extrude(context, id + "F9", {"entities" : qUnion([Q0]), "operationType" : NewBodyOperationType.REMOVE, "surfaceEntities" : qUnion([Q1]), "oppositeDirection" : true, "depth" : 2 * mm});
        }
    });
